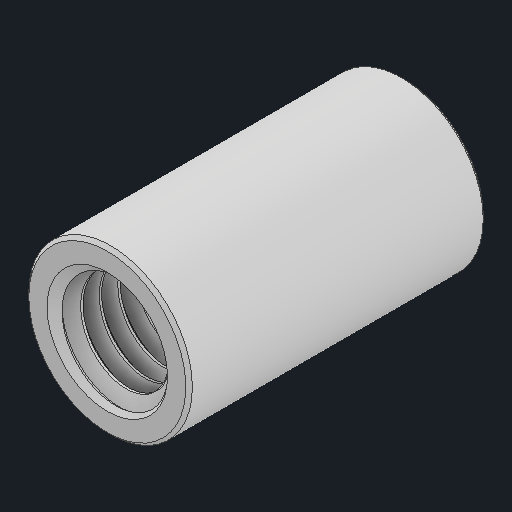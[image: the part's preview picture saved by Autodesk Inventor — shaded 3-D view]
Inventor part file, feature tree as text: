
AUTODESK INVENTOR PART (.ipt)
format: ipt  version: 2024 (Build 280153000, 153)  size: 529,408 bytes
history: native  units: in
note: dims shown in document units (in); Inventor stores cm internally (conversion verified against a paired STEP export)
features: mirror x1
ambient origin geometry x8: Origin, YZ Plane, XZ Plane, XY Plane, X Axis, Y Axis, Z Axis, Center Point
bodies: Solid1 (feature_tree)
feature tree (1):
  mirror  "Mirror1"
